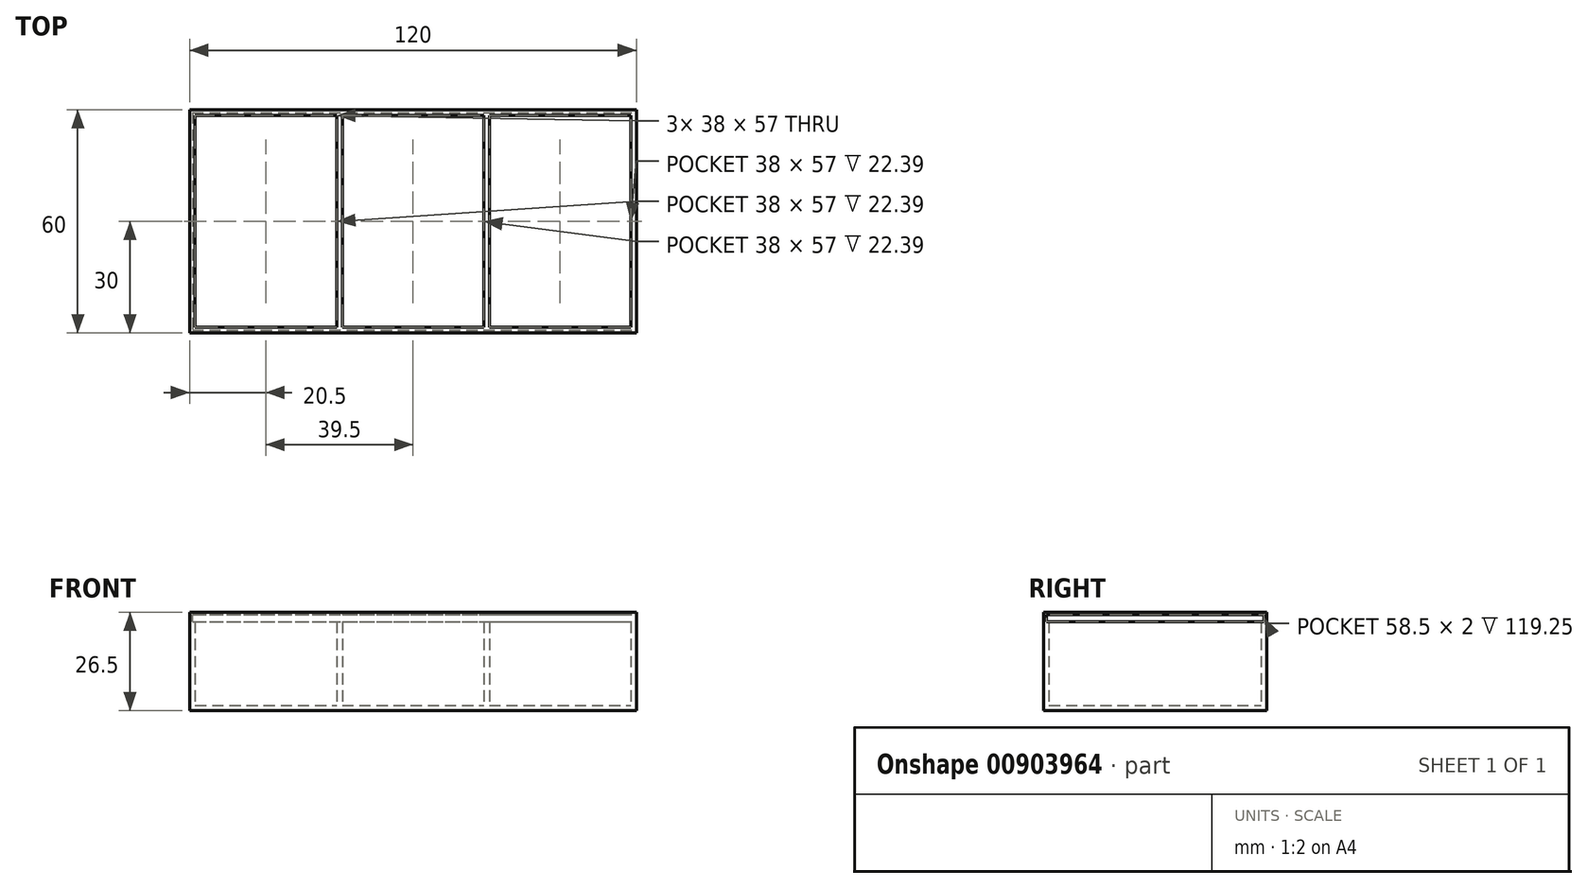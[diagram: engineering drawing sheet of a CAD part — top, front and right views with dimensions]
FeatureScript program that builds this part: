
annotation { "Feature Type Name" : "Feature", "Feature Type Description" : "" }
export const myFeature = defineFeature(function(context is Context, id is Id, definition is map)
    precondition{}
    {
        {
            var Q0;
            Q0=qCreatedBy(makeId("Top.planeOp"),FACE);
            var sketch = newSketch(context, id + "F0", { "sketchPlane" : qUnion([Q0])});
            skLineSegment(sketch, "E0.bottom", {"start": v(0, 0) * mm, "end": v(-120, 0) * mm});
            skLineSegment(sketch, "E0.top", {"start": v(0, -60) * mm, "end": v(-120, -60) * mm});
            skLineSegment(sketch, "E0.left", {"start": v(0, 0) * mm, "end": v(0, -60) * mm});
            skLineSegment(sketch, "E0.right", {"start": v(-120, 0) * mm, "end": v(-120, -60) * mm});
            skLineSegment(sketch, "E1", {"start": v(-118.5, -30) * mm, "end": v(-118.5, -58.5) * mm});
            skLineSegment(sketch, "E2", {"start": v(-118.5, -58.5) * mm, "end": v(-118.5, -1.5) * mm});
            skLineSegment(sketch, "E3", {"start": v(-60, -58.5) * mm, "end": v(-79, -58.5) * mm});
            skLineSegment(sketch, "E4", {"start": v(-118.5, -58.5) * mm, "end": v(-80.5, -58.5) * mm});
            skPoint(sketch, "E5.start.orphan", {"position": v(-120, -30) * mm});
            skPoint(sketch, "E6.start.orphan", {"position": v(-60, -60) * mm});
            skLineSegment(sketch, "E7", {"start": v(-1.5, -30) * mm, "end": v(-1.5, -58.5) * mm});
            skLineSegment(sketch, "E8", {"start": v(-1.5, -58.5) * mm, "end": v(-1.5, -1.5) * mm});
            skLineSegment(sketch, "E9", {"start": v(-60, -1.5) * mm, "end": v(-41, -1.5) * mm});
            skLineSegment(sketch, "E10", {"start": v(-1.5, -1.5) * mm, "end": v(-39.5, -1.5) * mm});
            skPoint(sketch, "E11.start.orphan", {"position": v(0, -30) * mm});
            skPoint(sketch, "E12.start.orphan", {"position": v(-60, 0) * mm});
            skLineSegment(sketch, "E13", {"start": v(-118.5, -1.5) * mm, "end": v(-80.5, -1.5) * mm});
            skLineSegment(sketch, "E14.left", {"start": v(-80.5, -1.5) * mm, "end": v(-80.5, -58.5) * mm});
            skLineSegment(sketch, "E14.right", {"start": v(-79, -1.5) * mm, "end": v(-79, -58.5) * mm});
            skLineSegment(sketch, "E15.trimOffspring", {"start": v(-80.5, -1.5) * mm, "end": v(-118.5, -1.5) * mm});
            skLineSegment(sketch, "E16.trimOffspring", {"start": v(-79, -58.5) * mm, "end": v(-41, -58.5) * mm});
            skLineSegment(sketch, "E17.trimOffspring", {"start": v(-80.5, -58.5) * mm, "end": v(-118.5, -58.5) * mm});
            skLineSegment(sketch, "E18", {"start": v(-79, -1.5) * mm, "end": v(-41, -1.5) * mm});
            skLineSegment(sketch, "E19.left", {"start": v(-41, -1.5) * mm, "end": v(-41, -58.5) * mm});
            skLineSegment(sketch, "E19.right", {"start": v(-39.5, -1.5) * mm, "end": v(-39.5, -58.5) * mm});
            skLineSegment(sketch, "E20.trimOffspring", {"start": v(-41, -1.5) * mm, "end": v(-79, -1.5) * mm});
            skLineSegment(sketch, "E21.trimOffspring", {"start": v(-39.5, -1.5) * mm, "end": v(-1.5, -1.5) * mm});
            skLineSegment(sketch, "E22.trimOffspring", {"start": v(-39.5, -58.5) * mm, "end": v(-1.5, -58.5) * mm});
            skSolve(sketch);
        }
        {
            var Q0;
            Q0=makeQuery(id+"F0.imprint","IMPRINT",FACE,{"disambiguationData":[TD([[makeQuery(id+"F0.imprint","IMPRINT",EDGE,{"derivedFrom":sQuery(id+"F0.wireOp",EDGE,"E0.bottom")}),1.0]])]});
            var Q1;
            Q1=makeQuery(id+"F0.imprint","IMPRINT",FACE,{"disambiguationData":[TD([[makeQuery(id+"F0.imprint","IMPRINT",EDGE,{"derivedFrom":sQuery(id+"F0.wireOp",EDGE,"E1")}),1.0]])]});
            var Q2;
            Q2=makeQuery(id+"F0.imprint","IMPRINT",FACE,{"disambiguationData":[TD([[makeQuery(id+"F0.imprint","IMPRINT",EDGE,{"derivedFrom":sQuery(id+"F0.wireOp",EDGE,"E3")}),-1.0]])]});
            var Q3;
            Q3=makeQuery(id+"F0.imprint","IMPRINT",FACE,{"disambiguationData":[TD([[makeQuery(id+"F0.imprint","IMPRINT",EDGE,{"derivedFrom":sQuery(id+"F0.wireOp",EDGE,"E7")}),-1.0]])]});
            extrude(context, id + "F1", {"entities" : qUnion([Q0, Q1, Q2, Q3]), "oppositeDirection" : true, "depth" : 1.5 * mm, "offsetDistance" : 25 * mm});
        }
        {
            var Q0;
            Q0=makeQuery(id+"F0.imprint","IMPRINT",FACE,{"disambiguationData":[TD([[makeQuery(id+"F0.imprint","IMPRINT",EDGE,{"derivedFrom":sQuery(id+"F0.wireOp",EDGE,"E0.bottom")}),1.0]])]});
            extrude(context, id + "F2", {"entities" : qUnion([Q0]), "operationType" : NewBodyOperationType.ADD, "depth" : 25 * mm, "offsetDistance" : 25 * mm});
        }
        {
            var Q0;
            Q0=qCreatedBy(makeId("Right.planeOp"),FACE);
            var sketch = newSketch(context, id + "F3", { "sketchPlane" : qUnion([Q0])});
            skLineSegment(sketch, "E23.bottom", {"start": v(-0.75, 24.4) * mm, "end": v(-59.25, 24.4) * mm});
            skLineSegment(sketch, "E23.top", {"start": v(-0.75, 22.4) * mm, "end": v(-59.25, 22.4) * mm});
            skLineSegment(sketch, "E24", {"start": v(-59.25, 23.4) * mm, "end": v(-59.25, 24.4) * mm});
            skLineSegment(sketch, "E25", {"start": v(-59.25, 24.4) * mm, "end": v(-59.25, 22.4) * mm});
            skPoint(sketch, "E26.start.orphan", {"position": v(-60, 23.4) * mm});
            skPoint(sketch, "E27.orphan", {"position": v(-60, 24.4) * mm});
            skPoint(sketch, "E28.orphan", {"position": v(-60, 22.4) * mm});
            skLineSegment(sketch, "E29", {"start": v(-0.75, 23.4) * mm, "end": v(-0.75, 22.4) * mm});
            skLineSegment(sketch, "E30", {"start": v(-0.75, 22.4) * mm, "end": v(-0.75, 24.4) * mm});
            skPoint(sketch, "E31.start.orphan", {"position": v(0, 23.4) * mm});
            skPoint(sketch, "E32.orphan", {"position": v(0, 24.4) * mm});
            skPoint(sketch, "E23.left.end.orphan", {"position": v(0, 22.4) * mm});
            skSolve(sketch);
        }
        {
            var Q0;
            Q0 = qSketchRegion(id + "F3", true);
            extrude(context, id + "F4", {"entities" : qUnion([Q0]), "operationType" : NewBodyOperationType.REMOVE, "oppositeDirection" : true, "depth" : 119.25 * mm, "offsetDistance" : 25 * mm});
        }
    });
